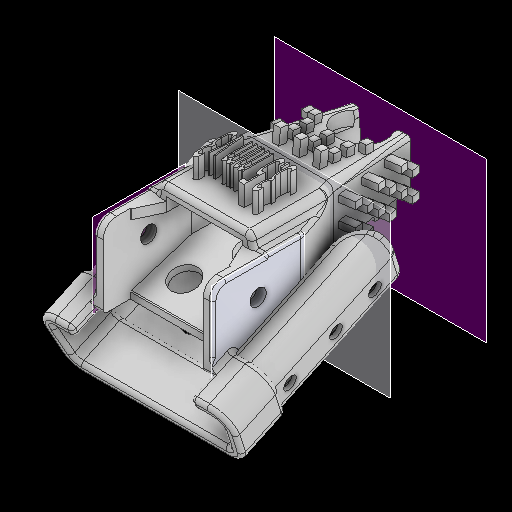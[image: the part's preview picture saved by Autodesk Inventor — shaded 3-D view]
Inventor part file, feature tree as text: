
AUTODESK INVENTOR PART (.ipt)
format: ipt  version: 2025 (Build 290162000, 162)  size: 3,648,512 bytes
history: native  units: mm
features: thicken_offset x73, sketch x24, projected_geometry x20, delete_face x13, hole x10, extrude x9, plane x7, fillet x7, other x3, loft x2, split x2, boolean_combine x2, thread x2, mirror x1, pattern_circular x1
ambient origin geometry x8: Origin, YZ Plane, XZ Plane, XY Plane, X Axis, Y Axis, Z Axis, Center Point
bodies: Solid1 (feature_tree), Solid8 (feature_tree), Solid2 (feature_tree), Solid4 (feature_tree), Solid5 (feature_tree), Solid6 (feature_tree), Solid7 (feature_tree)
feature tree (176):
  plane  "Work Plane6"
  loft  "Loft3"
  loft  "Loft4"
  fillet  "Fillet6"  [1 undecoded]
  sketch  "Sketch46"  dims[d284=0.0mm d287=0.45mm]
  extrude  "Grippers"  Depth=2.45mm
  mirror  "Mirror1"
  sketch  "Sketch47"  dims[d288=0.5mm d296=40.0mm d298=2.5mm d299=60.0mm d301=5.0mm d363=0.5mm d364=0.6mm d416=0.6mm d417=0.0mm d425=0.5mm]
  extrude  "FrontGrippers"  TaperAngle=0.0deg  [1 undecoded]
  sketch  "Sketch49"  dims[d426=60.0mm d428=5.0mm d429=10.0mm d431=10.0mm d433=20.0mm d435=1.5mm d436=20.0mm d438=1.5mm]
  extrude  "BackGrippers"  Depth=1.0mm TaperAngle=0.0deg
  plane  "Work Plane13"
  plane  "Work Plane14"
  extrude  "Extrusion16"  Depth=1.0mm TaperAngle=0.0deg
  extrude  "Extrusion19"  Depth=4.75mm
  extrude  "Extrusion21"  Depth=10.5mm
  extrude  "Extrusion22"  Depth=11.5mm
  plane  "Work Plane28"
  plane  "Work Plane29"
  split  "Split1"
  split  "Split2"
  extrude  "Extrusion34"  Depth=0.45mm
  boolean_combine  "Combine1"
  pattern_circular  "Circular Pattern1"  Count=4  [1 undecoded]
  delete_face  "Delete Face1"
  boolean_combine  "Combine2"
  thicken_offset  "Thicken1"
  thicken_offset  "Thicken2"
  thicken_offset  "Thicken3"
  fillet  "Fillet7"  Radius=0.5mm
  fillet  "Fillet8"  Radius=0.6mm
  fillet  "Fillet9"  Radius=0.6mm
  delete_face  "Delete Face2"
  delete_face  "Delete Face3"
  delete_face  "Delete Face4"
  delete_face  "Delete Face5"
  delete_face  "Delete Face6"
  delete_face  "Delete Face7"
  thicken_offset  "Thicken4"
  fillet  "Fillet10"  [1 undecoded]
  fillet  "Fillet11"  Radius=0.5mm
  hole  "Hole1"  [1 undecoded]
  hole  "Hole2"  [1 undecoded]
  hole  "Hole3"  [1 undecoded]
  hole  "Hole4"  [1 undecoded]
  hole  "Hole5"  [1 undecoded]
  hole  "Hole6"  [1 undecoded]
  thicken_offset  "Thicken5"
  thread  "Thread1"  [1 undecoded]
  thicken_offset  "Thicken6"
  thicken_offset  "Thicken7"
  thread  "Thread2"  [1 undecoded]
  thicken_offset  "Thicken8"
  thicken_offset  "Thicken9"
  thicken_offset  "Thicken10"
  thicken_offset  "Thicken11"
  thicken_offset  "Thicken12"
  thicken_offset  "Thicken13"
  thicken_offset  "Thicken14"
  thicken_offset  "Thicken15"
  thicken_offset  "Thicken16"
  thicken_offset  "Thicken17"
  thicken_offset  "Thicken18"
  thicken_offset  "Thicken19"
  thicken_offset  "Thicken20"
  thicken_offset  "Thicken21"
  thicken_offset  "Thicken22"
  thicken_offset  "Thicken23"
  thicken_offset  "Thicken24"
  thicken_offset  "Thicken25"
  thicken_offset  "Thicken26"
  thicken_offset  "Thicken27"
  thicken_offset  "Thicken28"
  thicken_offset  "Thicken29"
  thicken_offset  "Thicken30"
  thicken_offset  "Thicken31"
  thicken_offset  "Thicken32"
  thicken_offset  "Thicken33"
  thicken_offset  "Thicken34"
  thicken_offset  "Thicken35"
  thicken_offset  "Thicken36"
  extrude  "Extrusion35"  Depth=0.5mm
  hole  "Hole7"  [1 undecoded]
  delete_face  "Delete Face8"
  delete_face  "Delete Face9"
  delete_face  "Delete Face10"
  delete_face  "Delete Face11"
  delete_face  "Delete Face12"
  thicken_offset  "Thicken37"
  thicken_offset  "Thicken38"
  thicken_offset  "Thicken39"
  thicken_offset  "Thicken40"
  thicken_offset  "Thicken41"
  thicken_offset  "Thicken42"
  thicken_offset  "Thicken43"
  thicken_offset  "Thicken44"
  thicken_offset  "Thicken45"
  thicken_offset  "Thicken46"
  thicken_offset  "Thicken47"
  thicken_offset  "Thicken48"
  delete_face  "Delete Face13"
  thicken_offset  "Thicken49"
  thicken_offset  "Thicken50"
  thicken_offset  "Thicken51"
  thicken_offset  "Thicken52"
  thicken_offset  "Thicken53"
  thicken_offset  "Thicken54"
  thicken_offset  "Thicken55"
  thicken_offset  "Thicken56"
  thicken_offset  "Thicken57"
  thicken_offset  "Thicken58"
  thicken_offset  "Thicken59"
  thicken_offset  "Thicken60"
  thicken_offset  "Thicken61"
  thicken_offset  "Thicken62"
  thicken_offset  "Thicken63"
  thicken_offset  "Thicken64"
  thicken_offset  "Thicken65"
  thicken_offset  "Thicken66"
  thicken_offset  "Thicken67"
  thicken_offset  "Thicken68"
  thicken_offset  "Thicken69"
  thicken_offset  "Thicken70"
  thicken_offset  "Thicken71"
  thicken_offset  "Thicken72"
  thicken_offset  "Thicken73"
  fillet  "Fillet12"  Radius=2.0mm
  hole  "Hole8"  [1 undecoded]
  hole  "Hole9"  [1 undecoded]
  hole  "Hole10"  [1 undecoded]
  plane  "Work Plane4"
  plane  "Work Plane5"
  sketch  "Sketch5"  dims[d30=0.0mm d31=90.0deg d32=0.0mm d33=90.0deg]
  other  "Edges3"
  sketch  "Sketch7"  dims[d126=1.0mm d127=0.0mm d135=15.0mm d136=0.0mm]
  other  "Edges4"
  sketch  "Sketch22"  dims[d140=1.0mm d141=0.0mm d142=15.0mm d143=0.0mm]
  projected_geometry  "Projected Loop8"
  sketch  "Sketch25"  dims[d156=9.5mm d157=4.75mm]
  sketch  "Sketch27"  dims[d158=10.5mm d159=5.25mm]
  sketch  "Sketch28"  dims[d160=12.5mm d162=11.5mm]
  sketch  "Sketch Rectangular Pattern1"  dims[d20=-7.1mm d22=4.5mm]
  sketch  "Sketch Rectangular Pattern2"  dims[d23=3.5mm d24=0.0mm d25=90.0deg d26=0.0mm d27=90.0deg]
  sketch  "Sketch Rectangular Pattern3"  dims[d28=2.85mm d29=2.45mm]
  projected_geometry  "Projected Loop36"
  projected_geometry  "Projected Loop37"
  projected_geometry  "Projected Loop38"
  projected_geometry  "Projected Loop39"
  projected_geometry  "Projected Loop40"
  projected_geometry  "Projected Loop41"
  projected_geometry  "Projected Loop42"
  projected_geometry  "Projected Loop43"
  projected_geometry  "Projected Loop44"
  projected_geometry  "Projected Loop45"
  projected_geometry  "Projected Loop46"
  projected_geometry  "Projected Loop47"
  projected_geometry  "Projected Loop48"
  projected_geometry  "Projected Loop49"
  projected_geometry  "Projected Loop50"
  projected_geometry  "Projected Loop51"
  projected_geometry  "Projected Loop52"
  projected_geometry  "Projected Loop53"
  sketch  "Sketch50"  dims[d441=0.6mm d442=0.0mm]
  projected_geometry  "Projected Loop54"
  other  "Pattern of Solid6:1"
  sketch  "Sketch51"  dims[d444=6.25mm d445=5.75mm]
  sketch  "Sketch52"  dims[d447=0.25mm d448=0.0mm]
  sketch  "Sketch53"  dims[d449=0.0mm d450=7.5mm d451=0.0mm]
  sketch  "Sketch54"  dims[d452=20.0mm d453=4.363323mm d456=10.0mm d457=10.0mm d458=0.5mm]
  sketch  "Sketch55"  dims[d459=0.5mm d460=0.5mm]
  sketch  "Sketch56"  dims[d461=0.5mm d462=2.0mm d463=2.0mm]
  sketch  "Sketch57"  dims[d464=0.5mm d465=2.0mm]
  sketch  "Sketch58"  dims[d466=2.0mm d467=0.3mm]
  sketch  "Sketch59"  dims[d468=0.3mm]
  sketch  "Sketch60"  dims[d469=1.0mm d470=6.0mm d471=3.023mm d472=2.0mm d473=14.3117mm d474=1.0mm d475=0.0mm]
  sketch  "Sketch61"  dims[d476=1.0mm d477=6.0mm d478=4.0mm d479=2.0mm d480=90.0deg d481=1.0mm d482=0.0mm d483=1.0mm d484=6.0mm d485=4.0mm d486=2.0mm d487=90.0deg d488=1.0mm d489=0.0mm d490=1.0mm d491=6.0mm d492=4.0mm d493=2.0mm d494=90.0deg d495=1.0mm d496=0.0mm d497=1.5mm d498=6.0mm d499=4.0mm d500=2.0mm d501=90.0deg d502=1.0mm d503=0.0mm d504=1.5mm d505=6.0mm d506=4.0mm d507=2.0mm d508=90.0deg d509=1.0mm d510=0.0mm d511=0.2mm d512=0.2mm d513=0.7mm d514=0.0mm d515=0.2mm d516=0.2mm d517=0.2mm d518=0.2mm d519=0.7mm d520=0.0mm d521=0.2mm d522=0.2mm d523=1.0mm d524=1.0mm d525=1.0mm d526=1.0mm d527=1.0mm d528=1.0mm d529=1.0mm d530=1.0mm d531=1.0mm d532=1.0mm d533=1.0mm d534=1.0mm d535=1.0mm d536=1.0mm d537=1.0mm d538=1.0mm d539=1.0mm d540=1.0mm d541=1.0mm d542=1.0mm d543=1.0mm d544=1.0mm d545=1.0mm d546=1.0mm d547=1.0mm d548=1.0mm d549=1.0mm d550=1.0mm d551=1.0mm d552=1.0mm d553=1.0mm d554=1.0mm d555=1.0mm d556=1.0mm d557=1.0mm d558=1.0mm d559=1.0mm d560=1.0mm d561=1.0mm d562=1.0mm d563=1.0mm d564=1.0mm d565=1.0mm d566=1.0mm d567=1.0mm d568=1.0mm d569=1.0mm d570=1.0mm d571=1.0mm d572=1.0mm d573=1.0mm d574=1.0mm d575=1.0mm d576=1.0mm d577=1.0mm d578=1.0mm d579=1.5mm d580=0.0mm d581=3.5mm d582=6.0mm d583=4.0mm d584=2.0mm d585=90.0deg d586=1.0mm d587=0.0mm d588=0.5mm d589=0.5mm d590=0.5mm d591=0.5mm d592=0.5mm d593=0.5mm d594=0.5mm d595=0.5mm d596=0.5mm d597=0.5mm d598=0.5mm d599=0.5mm d600=0.5mm d601=0.5mm d602=0.5mm d603=0.5mm d604=0.5mm d605=0.5mm d606=0.5mm d607=0.5mm d608=0.5mm d609=0.5mm d610=0.5mm d611=0.5mm d612=0.5mm d613=0.5mm d614=0.5mm d615=0.5mm d616=0.5mm d617=0.5mm d618=0.5mm d619=0.5mm d620=0.5mm d621=0.5mm d622=0.5mm d623=0.5mm d624=0.5mm d625=0.5mm d626=0.5mm d627=0.5mm d628=0.5mm d629=0.5mm d630=0.5mm d631=0.5mm d632=0.5mm d633=0.5mm d634=0.5mm d635=0.5mm d636=0.5mm d637=0.5mm d638=0.5mm d639=0.5mm d640=0.5mm d641=0.5mm d642=0.5mm d643=0.5mm d644=0.5mm d645=0.5mm d646=0.5mm d647=0.5mm d648=0.5mm d649=0.5mm d650=0.5mm d651=0.5mm d652=0.5mm d653=0.5mm d654=0.4mm d655=0.4mm d656=0.4mm d657=0.4mm d658=0.4mm d659=0.4mm d660=0.4mm d661=0.4mm d662=0.3mm d663=2.0mm d664=6.0mm d665=4.0mm d666=2.0mm d667=90.0deg d668=5.75mm d669=0.0mm d670=2.0mm d671=6.0mm d672=4.0mm d673=2.0mm d674=90.0deg d675=5.75mm d676=0.0mm d677=2.0mm d678=6.0mm d679=4.0mm d680=2.0mm d681=90.0deg d682=5.75mm d683=0.0mm d39=0.5mm d40=0.872665mm d41=0.5mm d42=0.872665mm d193=0.5mm d194=0.872665mm d195=0.5mm d196=0.872665mm]
note: 16 required parameter values undecoded (feature->parameter linkage not recoverable at this tier; creation-order binding heuristic only, values carry confidence <= 0.55)
